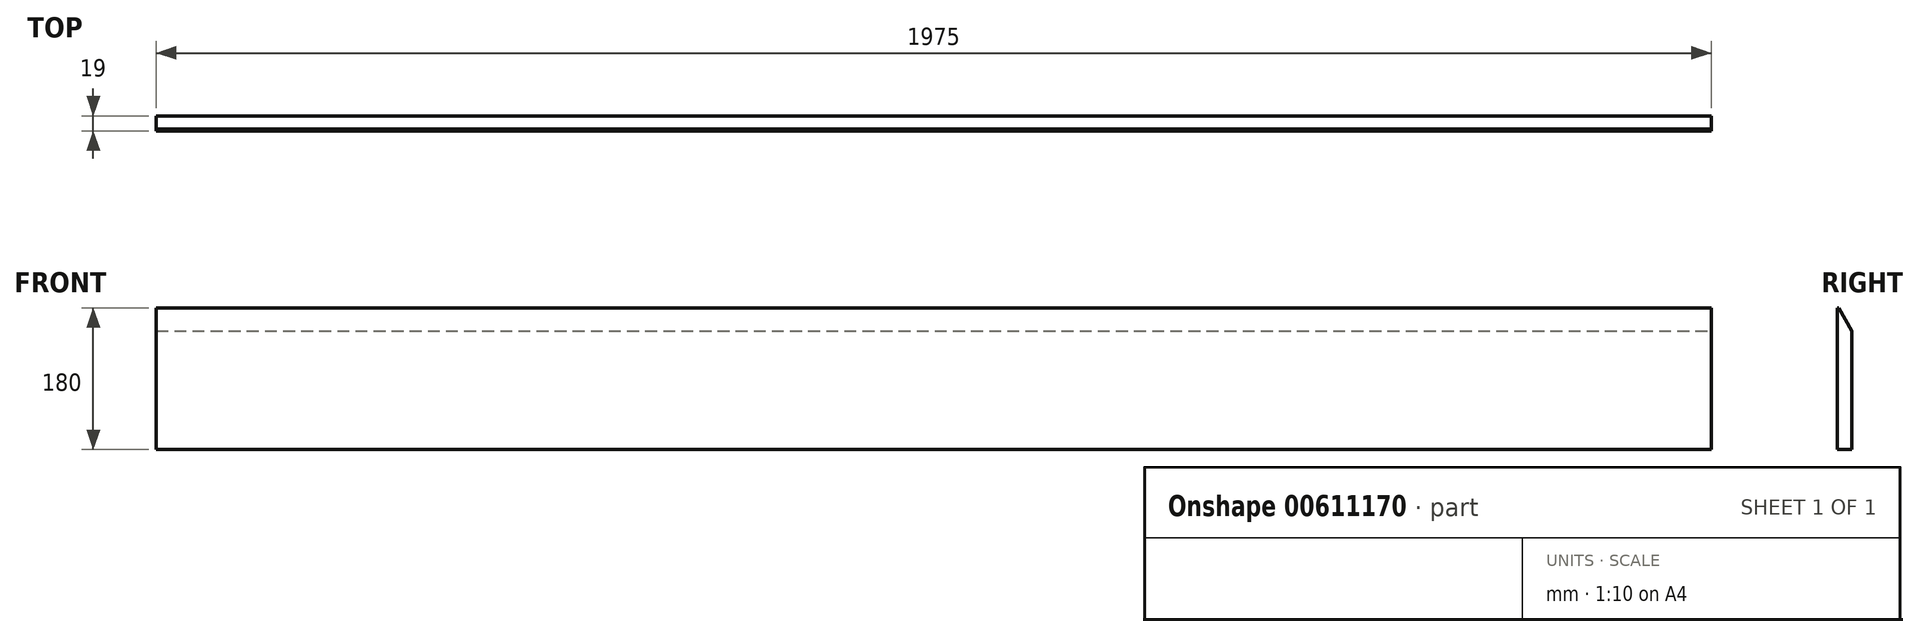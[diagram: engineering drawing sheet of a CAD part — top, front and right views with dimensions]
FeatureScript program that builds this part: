
annotation { "Feature Type Name" : "Feature", "Feature Type Description" : "" }
export const myFeature = defineFeature(function(context is Context, id is Id, definition is map)
    precondition{}
    {
        {
            var Q0;
            Q0=qCreatedBy(makeId("Front.planeOp"),FACE);
            var sketch = newSketch(context, id + "F0", { "sketchPlane" : qUnion([Q0])});
            skLineSegment(sketch, "E0.bottom", {"start": v(0, 0) * mm, "end": v(1975, 0) * mm});
            skLineSegment(sketch, "E0.top", {"start": v(0, 180) * mm, "end": v(1975, 180) * mm});
            skLineSegment(sketch, "E0.left", {"start": v(0, 0) * mm, "end": v(0, 180) * mm});
            skLineSegment(sketch, "E0.right", {"start": v(1975, 0) * mm, "end": v(1975, 180) * mm});
            skSolve(sketch);
        }
        {
            var Q0;
            Q0=makeQuery(id+"F0.imprint","IMPRINT",FACE,{"disambiguationData":[TD([[makeQuery(id+"F0.imprint","IMPRINT",EDGE,{"derivedFrom":sQuery(id+"F0.wireOp",EDGE,"E0.bottom")}),1.0]])]});
            extrude(context, id + "F1", {"entities" : qUnion([Q0]), "depth" : 19 * mm, "offsetDistance" : 25 * mm});
        }
        {
            var Q0;
            Q0=makeQuery(id+"F1.opExtrude","CAP_EDGE",EDGE,{"disambiguationData":[OSD([sQuery(id+"F0.wireOp",EDGE,"E0.top")])],"isStart":true});
            chamfer(context, id + "F2", {"entities" : qUnion([Q0]), "chamferType" : ChamferType.OFFSET_ANGLE, "width" : 17 * mm, "oppositeDirection" : true, "angle" : 60 * degree, "tangentPropagation" : true});
        }
    });
